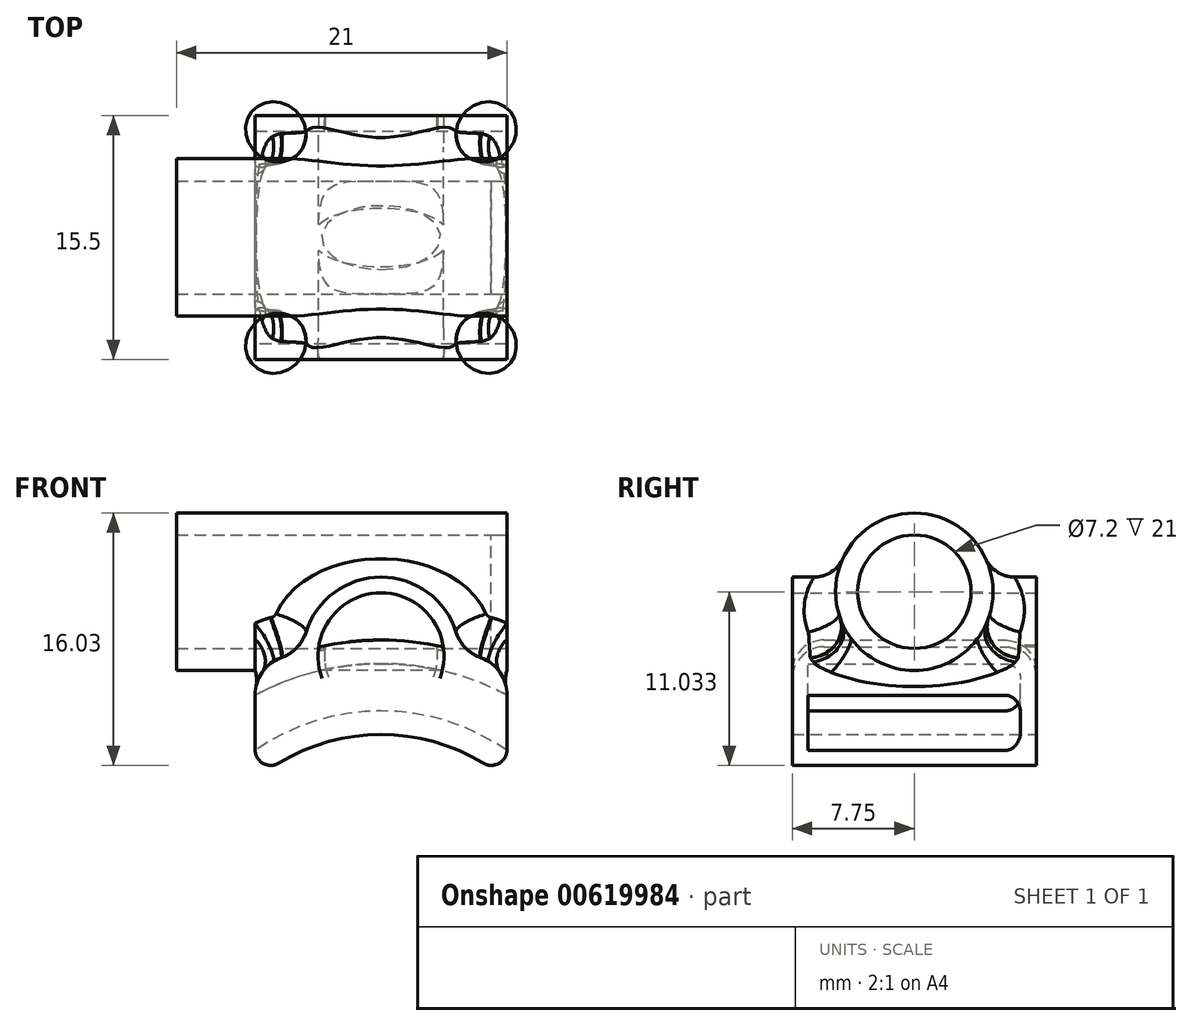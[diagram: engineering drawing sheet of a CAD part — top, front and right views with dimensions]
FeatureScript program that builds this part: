
annotation { "Feature Type Name" : "Feature", "Feature Type Description" : "" }
export const myFeature = defineFeature(function(context is Context, id is Id, definition is map)
    precondition{}
    {
        {
            var Q0;
            Q0=qCreatedBy(makeId("Front.planeOp"),FACE);
            var sketch = newSketch(context, id + "F0", { "sketchPlane" : qUnion([Q0])});
            skArc(sketch, "E0", {"start": v(8, 9.6) * mm, "mid": v(0, 12.5) * mm, "end": v(-8, 9.6) * mm});
            skArc(sketch, "E1.0", {"start": v(8, 11.49) * mm, "mid": v(0, 14) * mm, "end": v(-8, 11.49) * mm});
            skLineSegment(sketch, "E2", {"start": v(-8, 11.49) * mm, "end": v(-8, 9.6) * mm});
            skLineSegment(sketch, "E3", {"start": v(8, 11.49) * mm, "end": v(8, 9.6) * mm});
            skArc(sketch, "E4.0", {"start": v(8, 15) * mm, "mid": v(0, 17) * mm, "end": v(-8, 15) * mm});
            skLineSegment(sketch, "E5", {"start": v(-8, 15) * mm, "end": v(-8, 16.68) * mm});
            skLineSegment(sketch, "E6", {"start": v(8, 15) * mm, "end": v(8, 16.68) * mm});
            skArc(sketch, "E7.0", {"start": v(8, 16.68) * mm, "mid": v(0, 18.5) * mm, "end": v(-8, 16.68) * mm});
            skPoint(sketch, "E8.end.orphan", {"position": v(-8, 29.56) * mm});
            skPoint(sketch, "E8.start.orphan", {"position": v(8, 29.56) * mm});
            skArc(sketch, "E9", {"start": v(5, 17.81) * mm, "mid": v(0, 22.5) * mm, "end": v(-5, 17.81) * mm});
            skPoint(sketch, "E9.centerSnap0", {"position": v(0, 17) * mm});
            skArc(sketch, "E10.0", {"start": v(3.96, 18.07) * mm, "mid": v(0, 21.5) * mm, "end": v(-3.96, 18.07) * mm});
            skSolve(sketch);
        }
        {
            var Q0;
            Q0=qSketchRegion(id+"F0",true);
            extrude(context, id + "F1", {"entities" : qUnion([Q0]), "depth" : 13.5 * mm, "offsetDistance" : 25 * mm});
        }
        {
            var Q0;
            Q0=makeQuery(id+"F1.opExtrude","CAP_FACE",FACE,{"disambiguationData":[OSD([sQuery(id+"F0.wireOp",EDGE,"E0"),sQuery(id+"F0.wireOp",EDGE,"E1.0"),sQuery(id+"F0.wireOp",EDGE,"E2"),sQuery(id+"F0.wireOp",EDGE,"E3")])],"isStart":true});
            var sketch = newSketch(context, id + "F2", { "sketchPlane" : qUnion([Q0])});
            skCircle(sketch, "E11", {"center": v(0, 17.5) * mm, "radius": 3.6 * mm});
            skPoint(sketch, "E11.centerSnap0", {"position": v(0, 14) * mm});
            skCircle(sketch, "E12", {"center": v(0, 17.5) * mm, "radius": 5 * mm});
            skSolve(sketch);
        }
        {
            var Q0;
            Q0=qSketchRegion(id+"F2",true);
            extrude(context, id + "F3", {"entities" : qUnion([Q0]), "depth" : 1 * mm, "offsetDistance" : 25 * mm});
        }
        {
            var Q0;
            Q0=makeQuery(id+"F1.opExtrude","CAP_FACE",FACE,{"disambiguationData":[OSD([sQuery(id+"F0.wireOp",EDGE,"E4.0"),sQuery(id+"F0.wireOp",EDGE,"E5"),sQuery(id+"F0.wireOp",EDGE,"E6"),sQuery(id+"F0.wireOp",EDGE,"E7.0"),sQuery(id+"F0.wireOp",EDGE,"E9"),sQuery(id+"F0.wireOp",EDGE,"E10.0")])],"isStart":true});
            var sketch = newSketch(context, id + "F4", { "sketchPlane" : qUnion([Q0])});
            skArc(sketch, "E13.0", {"start": v(-3.54, 18.16) * mm, "mid": v(0, 13.9) * mm, "end": v(3.54, 18.16) * mm});
            skArc(sketch, "E14.0", {"start": v(-3.54, 18.16) * mm, "mid": v(0, 18.5) * mm, "end": v(3.54, 18.16) * mm});
            skSolve(sketch);
        }
        {
            var Q0;
            Q0=qSketchRegion(id+"F4",true);
            extrude(context, id + "F5", {"entities" : qUnion([Q0]), "depth" : 1 * mm, "offsetDistance" : 25 * mm});
        }
        {
            var Q0;
            Q0=makeQuery(id+"F1.opExtrude","CAP_FACE",FACE,{"disambiguationData":[OSD([sQuery(id+"F0.wireOp",EDGE,"E0"),sQuery(id+"F0.wireOp",EDGE,"E1.0"),sQuery(id+"F0.wireOp",EDGE,"E2"),sQuery(id+"F0.wireOp",EDGE,"E3")])],"isStart":true});
            var sketch = newSketch(context, id + "F6", { "sketchPlane" : qUnion([Q0])});
            skLineSegment(sketch, "E15.0", {"start": v(-8, 11.49) * mm, "end": v(-8, 9.6) * mm});
            skLineSegment(sketch, "E15.2", {"start": v(8, 9.6) * mm, "end": v(8, 11.49) * mm});
            skArc(sketch, "E15.3", {"start": v(-8, 9.6) * mm, "mid": v(0, 12.5) * mm, "end": v(8, 9.6) * mm});
            skArc(sketch, "E16.0", {"start": v(-8, 16.68) * mm, "mid": v(-6.52, 17.31) * mm, "end": v(-5, 17.81) * mm});
            skArc(sketch, "E17.0", {"start": v(5, 17.81) * mm, "mid": v(6.52, 17.31) * mm, "end": v(8, 16.68) * mm});
            skLineSegment(sketch, "E18.0", {"start": v(-8, 15) * mm, "end": v(-8, 16.68) * mm});
            skLineSegment(sketch, "E19.0", {"start": v(8, 15) * mm, "end": v(8, 16.68) * mm});
            skArc(sketch, "E20.0", {"start": v(-5, 17.81) * mm, "mid": v(0, 12.5) * mm, "end": v(5, 17.81) * mm});
            skLineSegment(sketch, "E21", {"start": v(-8, 15) * mm, "end": v(-8, 11.49) * mm});
            skLineSegment(sketch, "E22", {"start": v(8, 15) * mm, "end": v(8, 11.49) * mm});
            skSolve(sketch);
        }
        {
            var Q0;
            Q0=qSketchRegion(id+"F6",true);
            extrude(context, id + "F7", {"entities" : qUnion([Q0]), "depth" : 1 * mm, "offsetDistance" : 25 * mm});
        }
        {
            var Q0;
            Q0=makeQuery(id+"F1.opExtrude","CAP_FACE",FACE,{"disambiguationData":[OSD([sQuery(id+"F0.wireOp",EDGE,"E0"),sQuery(id+"F0.wireOp",EDGE,"E1.0"),sQuery(id+"F0.wireOp",EDGE,"E2"),sQuery(id+"F0.wireOp",EDGE,"E3")])],"isStart":false});
            var sketch = newSketch(context, id + "F8", { "sketchPlane" : qUnion([Q0])});
            skArc(sketch, "E23.0", {"start": v(8, 9.6) * mm, "mid": v(0, 12.5) * mm, "end": v(-8, 9.6) * mm});
            skArc(sketch, "E24.0", {"start": v(8, 16.68) * mm, "mid": v(0, 18.5) * mm, "end": v(-8, 16.68) * mm});
            skLineSegment(sketch, "E25", {"start": v(-8, 9.6) * mm, "end": v(-8, 16.68) * mm});
            skLineSegment(sketch, "E26", {"start": v(8, 9.6) * mm, "end": v(8, 16.68) * mm});
            skArc(sketch, "E27.0", {"start": v(5, 17.81) * mm, "mid": v(0, 22.5) * mm, "end": v(-5, 17.81) * mm});
            skArc(sketch, "E28.0", {"start": v(3.96, 18.07) * mm, "mid": v(0, 21.5) * mm, "end": v(-3.96, 18.07) * mm});
            skSolve(sketch);
        }
        {
            var Q0;
            Q0=qSketchRegion(id+"F8",true);
            extrude(context, id + "F9", {"entities" : qUnion([Q0]), "depth" : 1 * mm, "offsetDistance" : 25 * mm});
        }
        {
            var Q0;
            Q0=makeQuery(id+"F1.opExtrude","SWEPT_BODY",BODY,{"disambiguationData":[OSD([sQuery(id+"F0.wireOp",EDGE,"E4.0"),sQuery(id+"F0.wireOp",EDGE,"E5"),sQuery(id+"F0.wireOp",EDGE,"E6"),sQuery(id+"F0.wireOp",EDGE,"E7.0"),sQuery(id+"F0.wireOp",EDGE,"E9"),sQuery(id+"F0.wireOp",EDGE,"E10.0")])]});
            var Q1;
            Q1=makeQuery(id+"F3.opExtrude","SWEPT_BODY",BODY,{"disambiguationData":[OSD([sQuery(id+"F2.wireOp",EDGE,"E11"),sQuery(id+"F2.wireOp",EDGE,"E12")])]});
            var Q2;
            Q2=makeQuery(id+"F1.opExtrude","SWEPT_BODY",BODY,{"disambiguationData":[OSD([sQuery(id+"F0.wireOp",EDGE,"E0"),sQuery(id+"F0.wireOp",EDGE,"E1.0"),sQuery(id+"F0.wireOp",EDGE,"E2"),sQuery(id+"F0.wireOp",EDGE,"E3")])]});
            var Q3;
            Q3=makeQuery(id+"F7.opExtrude","SWEPT_BODY",BODY,{"disambiguationData":[OSD([sQuery(id+"F6.wireOp",EDGE,"E15.2"),sQuery(id+"F6.wireOp",EDGE,"E15.3"),sQuery(id+"F6.wireOp",EDGE,"E17.0"),sQuery(id+"F6.wireOp",EDGE,"E19.0"),sQuery(id+"F6.wireOp",EDGE,"E20.0"),sQuery(id+"F6.wireOp",EDGE,"E22")])]});
            var Q4;
            Q4=makeQuery(id+"F7.opExtrude","SWEPT_BODY",BODY,{"disambiguationData":[OSD([sQuery(id+"F6.wireOp",EDGE,"E15.0"),sQuery(id+"F6.wireOp",EDGE,"E15.3"),sQuery(id+"F6.wireOp",EDGE,"E16.0"),sQuery(id+"F6.wireOp",EDGE,"E18.0"),sQuery(id+"F6.wireOp",EDGE,"E20.0"),sQuery(id+"F6.wireOp",EDGE,"E21")])]});
            var Q5;
            Q5=makeQuery(id+"F5.opExtrude","SWEPT_BODY",BODY,{"disambiguationData":[OSD([sQuery(id+"F4.wireOp",EDGE,"E13.0"),sQuery(id+"F4.wireOp",EDGE,"E14.0")])]});
            var Q6;
            Q6=makeQuery(id+"F9.opExtrude","SWEPT_BODY",BODY,{"disambiguationData":[OSD([sQuery(id+"F8.wireOp",EDGE,"E23.0"),sQuery(id+"F8.wireOp",EDGE,"E24.0"),sQuery(id+"F8.wireOp",EDGE,"E25"),sQuery(id+"F8.wireOp",EDGE,"E26")])]});
            booleanBodies(context, id + "F10", {"operationType" : BooleanOperationType.UNION, "tools" : qUnion([Q0, Q1, Q2, Q3, Q4, Q5, Q6])});
        }
        {
            var Q0;
            Q0=makeQuery(id+"F5.opExtrude","CAP_EDGE",EDGE,{"disambiguationData":[OSD([sQuery(id+"F4.wireOp",EDGE,"E14.0")])],"isStart":false});
            var Q1;
            {var subQ0=sQuery(id+"F8.wireOp",EDGE,"E28.0");var subQ1=sQuery(id+"F8.wireOp",EDGE,"E24.0");Q1=makeQuery(id+"F9.opExtrude","CAP_EDGE",EDGE,{"disambiguationData":[OSD([subQ1]),TDD([makeQuery(id+"F8.imprint","IMPRINT",EDGE,{"disambiguationData":[TD([[makeQuery(id+"F8.imprint","INTERSECT",VERTEX,{"disambiguationData":[OD(0.0)],"derivedFrom":[subQ1,subQ0]}),-1.0]])],"derivedFrom":subQ1})])],"isStart":false});}
            fillet(context, id + "F11", {"entities" : qUnion([Q0, Q1]), "radius" : 2 * mm, "tangentPropagation" : true, "allowEdgeOverflow" : false});
        }
        {
            var Q0;
            {var subQ0=sQuery(id+"F0.wireOp",EDGE,"E9");var subQ1=sQuery(id+"F0.wireOp",EDGE,"E7.0");Q0=makeQuery(id+"F10.opBoolean","MERGE",EDGE,{"derivedFrom":[makeQuery(id+"F1.opExtrude","SWEPT_EDGE",EDGE,{"disambiguationData":[OSD([subQ1,subQ0]),TDD([makeQuery(id+"F0.imprint","INTERSECT",VERTEX,{"disambiguationData":[OD(1.0)],"derivedFrom":[subQ1,subQ0]})])]}),makeQuery(id+"F7.opExtrude","SWEPT_EDGE",EDGE,{"disambiguationData":[OSD([sQuery(id+"F6.wireOp",EDGE,"E17.0"),sQuery(id+"F6.wireOp",EDGE,"E20.0")])]})]});}
            var Q1;
            Q1=makeQuery(id+"F10.opBoolean","MERGE",EDGE,{"derivedFrom":[makeQuery(id+"F1.opExtrude","SWEPT_EDGE",EDGE,{"disambiguationData":[OSD([sQuery(id+"F0.wireOp",EDGE,"E5"),sQuery(id+"F0.wireOp",EDGE,"E7.0")])]}),makeQuery(id+"F7.opExtrude","SWEPT_EDGE",EDGE,{"disambiguationData":[OSD([sQuery(id+"F6.wireOp",EDGE,"E17.0"),sQuery(id+"F6.wireOp",EDGE,"E19.0")])]}),makeQuery(id+"F9.opExtrude","SWEPT_EDGE",EDGE,{"disambiguationData":[OSD([sQuery(id+"F8.wireOp",EDGE,"E24.0"),sQuery(id+"F8.wireOp",EDGE,"E25")])]})]});
            var Q2;
            {var subQ0=sQuery(id+"F0.wireOp",EDGE,"E9");var subQ1=sQuery(id+"F0.wireOp",EDGE,"E7.0");Q2=makeQuery(id+"F10.opBoolean","MERGE",EDGE,{"derivedFrom":[makeQuery(id+"F1.opExtrude","SWEPT_EDGE",EDGE,{"disambiguationData":[OSD([subQ1,subQ0]),TDD([makeQuery(id+"F0.imprint","INTERSECT",VERTEX,{"disambiguationData":[OD(0.0)],"derivedFrom":[subQ1,subQ0]})])]}),makeQuery(id+"F7.opExtrude","SWEPT_EDGE",EDGE,{"disambiguationData":[OSD([sQuery(id+"F6.wireOp",EDGE,"E16.0"),sQuery(id+"F6.wireOp",EDGE,"E20.0")])]})]});}
            var Q3;
            Q3=makeQuery(id+"F10.opBoolean","MERGE",EDGE,{"derivedFrom":[makeQuery(id+"F1.opExtrude","SWEPT_EDGE",EDGE,{"disambiguationData":[OSD([sQuery(id+"F0.wireOp",EDGE,"E6"),sQuery(id+"F0.wireOp",EDGE,"E7.0")])]}),makeQuery(id+"F7.opExtrude","SWEPT_EDGE",EDGE,{"disambiguationData":[OSD([sQuery(id+"F6.wireOp",EDGE,"E16.0"),sQuery(id+"F6.wireOp",EDGE,"E18.0")])]}),makeQuery(id+"F9.opExtrude","SWEPT_EDGE",EDGE,{"disambiguationData":[OSD([sQuery(id+"F8.wireOp",EDGE,"E24.0"),sQuery(id+"F8.wireOp",EDGE,"E26")])]})]});
            fillet(context, id + "F12", {"entities" : qUnion([Q0, Q1, Q2, Q3]), "radius" : 2.5 * mm, "tangentPropagation" : true, "allowEdgeOverflow" : false});
        }
        {
            var Q0;
            Q0=makeQuery(id+"F10.opBoolean","MERGE",EDGE,{"derivedFrom":[makeQuery(id+"F1.opExtrude","SWEPT_EDGE",EDGE,{"disambiguationData":[OSD([sQuery(id+"F0.wireOp",EDGE,"E0"),sQuery(id+"F0.wireOp",EDGE,"E2")])]}),makeQuery(id+"F7.opExtrude","SWEPT_EDGE",EDGE,{"disambiguationData":[OSD([sQuery(id+"F6.wireOp",EDGE,"E15.2"),sQuery(id+"F6.wireOp",EDGE,"E15.3")])]}),makeQuery(id+"F9.opExtrude","SWEPT_EDGE",EDGE,{"disambiguationData":[OSD([sQuery(id+"F8.wireOp",EDGE,"E23.0"),sQuery(id+"F8.wireOp",EDGE,"E25")])]})]});
            var Q1;
            Q1=makeQuery(id+"F10.opBoolean","MERGE",EDGE,{"derivedFrom":[makeQuery(id+"F1.opExtrude","SWEPT_EDGE",EDGE,{"disambiguationData":[OSD([sQuery(id+"F0.wireOp",EDGE,"E0"),sQuery(id+"F0.wireOp",EDGE,"E3")])]}),makeQuery(id+"F7.opExtrude","SWEPT_EDGE",EDGE,{"disambiguationData":[OSD([sQuery(id+"F6.wireOp",EDGE,"E15.0"),sQuery(id+"F6.wireOp",EDGE,"E15.3")])]}),makeQuery(id+"F9.opExtrude","SWEPT_EDGE",EDGE,{"disambiguationData":[OSD([sQuery(id+"F8.wireOp",EDGE,"E23.0"),sQuery(id+"F8.wireOp",EDGE,"E26")])]})]});
            fillet(context, id + "F13", {"entities" : qUnion([Q0, Q1]), "radius" : 1 * mm, "tangentPropagation" : true, "allowEdgeOverflow" : false});
        }
        {
            var Q0;
            {var subQ0=sQuery(id+"F6.wireOp",EDGE,"E20.0");var subQ1=sQuery(id+"F6.wireOp",EDGE,"E15.3");Q0=makeQuery(id+"F10.opBoolean","INTERSECT",EDGE,{"derivedFrom":[makeQuery(id+"F3.opExtrude","CAP_FACE",FACE,{"disambiguationData":[OSD([sQuery(id+"F2.wireOp",EDGE,"E11"),sQuery(id+"F2.wireOp",EDGE,"E12")])],"isStart":true}),makeQuery(id+"F5.opExtrude","CAP_FACE",FACE,{"disambiguationData":[OSD([sQuery(id+"F4.wireOp",EDGE,"E13.0"),sQuery(id+"F4.wireOp",EDGE,"E14.0")])],"isStart":true}),makeQuery(id+"F7.opExtrude","CAP_FACE",FACE,{"disambiguationData":[OSD([sQuery(id+"F6.wireOp",EDGE,"E15.0"),subQ1,sQuery(id+"F6.wireOp",EDGE,"E16.0"),sQuery(id+"F6.wireOp",EDGE,"E18.0"),subQ0,sQuery(id+"F6.wireOp",EDGE,"E21")])],"isStart":true}),makeQuery(id+"F7.opExtrude","CAP_FACE",FACE,{"disambiguationData":[OSD([sQuery(id+"F6.wireOp",EDGE,"E15.2"),subQ1,sQuery(id+"F6.wireOp",EDGE,"E17.0"),sQuery(id+"F6.wireOp",EDGE,"E19.0"),subQ0,sQuery(id+"F6.wireOp",EDGE,"E22")])],"isStart":true})]});}
            var Q1;
            Q1=makeQuery(id+"F1.opExtrude","CAP_EDGE",EDGE,{"disambiguationData":[OSD([sQuery(id+"F0.wireOp",EDGE,"E4.0")])],"isStart":true});
            var Q2;
            Q2=makeQuery(id+"F1.opExtrude","CAP_EDGE",EDGE,{"disambiguationData":[OSD([sQuery(id+"F0.wireOp",EDGE,"E1.0")])],"isStart":false});
            var Q3;
            Q3=makeQuery(id+"F1.opExtrude","CAP_EDGE",EDGE,{"disambiguationData":[OSD([sQuery(id+"F0.wireOp",EDGE,"E4.0")])],"isStart":false});
            fillet(context, id + "F14", {"entities" : qUnion([Q0, Q1, Q2, Q3]), "radius" : 1 * mm, "tangentPropagation" : true, "allowEdgeOverflow" : false});
        }
        {
            var Q0;
            Q0=qCreatedBy(makeId("Right.planeOp"),FACE);
            var sketch = newSketch(context, id + "F15", { "sketchPlane" : qUnion([Q0])});
            skCircle(sketch, "E29", {"center": v(-6.75, 21.57) * mm, "radius": 5 * mm});
            skSolve(sketch);
        }
        {
            var Q0;
            Q0=qSketchRegion(id+"F15",true);
            extrude(context, id + "F16", {"entities" : qUnion([Q0]), "operationType" : NewBodyOperationType.ADD, "endBound" : BoundingType.SYMMETRIC, "depth" : 16 * mm, "offsetDistance" : 25 * mm});
        }
        {
            var Q0;
            Q0=makeQuery(id+"F16.opExtrude","CAP_FACE",FACE,{"disambiguationData":[OSD([sQuery(id+"F15.wireOp",EDGE,"E29")])],"isStart":false});
            var sketch = newSketch(context, id + "F17", { "sketchPlane" : qUnion([Q0])});
            skCircle(sketch, "E30", {"center": v(-6.75, 21.57) * mm, "radius": 3.6 * mm});
            skSolve(sketch);
        }
        {
            var Q0;
            Q0=qSketchRegion(id+"F17",true);
            extrude(context, id + "F18", {"entities" : qUnion([Q0]), "operationType" : NewBodyOperationType.REMOVE, "endBound" : BoundingType.THROUGH_ALL, "oppositeDirection" : true, "depth" : 25 * mm, "offsetDistance" : 25 * mm});
        }
        {
            var Q0;
            Q0=makeQuery(id+"F9.opExtrude","CAP_FACE",FACE,{"disambiguationData":[OSD([sQuery(id+"F8.wireOp",EDGE,"E23.0"),sQuery(id+"F8.wireOp",EDGE,"E24.0"),sQuery(id+"F8.wireOp",EDGE,"E25"),sQuery(id+"F8.wireOp",EDGE,"E26"),sQuery(id+"F8.wireOp",EDGE,"E27.0"),sQuery(id+"F8.wireOp",EDGE,"E28.0")])],"isStart":false});
            var sketch = newSketch(context, id + "F19", { "sketchPlane" : qUnion([Q0])});
            skLineSegment(sketch, "E31", {"start": v(0, 27.62) * mm, "end": v(0, 5.28) * mm});
            skArc(sketch, "E32.0", {"start": v(-3.96, 18.07) * mm, "mid": v(0, 18.5) * mm, "end": v(3.96, 18.07) * mm});
            skArc(sketch, "E33.0", {"start": v(3.96, 18.07) * mm, "mid": v(0, 21.5) * mm, "end": v(-3.96, 18.07) * mm});
            skSolve(sketch);
        }
        {
            var Q0;
            Q0=qSketchRegion(id+"F19",true);
            extrude(context, id + "F20", {"entities" : qUnion([Q0]), "operationType" : NewBodyOperationType.REMOVE, "endBound" : BoundingType.THROUGH_ALL, "oppositeDirection" : true, "depth" : 25 * mm, "offsetDistance" : 25 * mm});
        }
        {
            var Q0;
            Q0=makeQuery(id+"F16.boolean.opBoolean","INTERSECT",EDGE,{"disambiguationData":[OD(1.0)],"derivedFrom":[makeQuery(id+"F10.opBoolean","MERGE",FACE,{"derivedFrom":[makeQuery(id+"F1.opExtrude","SWEPT_FACE",FACE,{"disambiguationData":[OSD([sQuery(id+"F0.wireOp",EDGE,"E9")])]}),makeQuery(id+"F3.opExtrude","SWEPT_FACE",FACE,{"disambiguationData":[OSD([sQuery(id+"F2.wireOp",EDGE,"E12")])]}),makeQuery(id+"F9.opExtrude","SWEPT_FACE",FACE,{"disambiguationData":[OSD([sQuery(id+"F8.wireOp",EDGE,"E27.0")])]})]}),makeQuery(id+"F16.opExtrude","SWEPT_FACE",FACE,{"disambiguationData":[OSD([sQuery(id+"F15.wireOp",EDGE,"E29")])]})]});
            fillet(context, id + "F21", {"entities" : qUnion([Q0]), "radius" : 2 * mm, "tangentPropagation" : true, "allowEdgeOverflow" : false});
        }
        {
            var Q0;
            Q0=makeQuery(id+"F16.opExtrude","CAP_FACE",FACE,{"disambiguationData":[OSD([sQuery(id+"F15.wireOp",EDGE,"E29")])],"isStart":false});
            var sketch = newSketch(context, id + "F22", { "sketchPlane" : qUnion([Q0])});
            skCircle(sketch, "E34.0", {"center": v(-6.75, 21.57) * mm, "radius": 3.6 * mm});
            skSolve(sketch);
        }
        {
            var Q0;
            Q0 = qSketchRegion(id + "F22", true);
            extrude(context, id + "F23", {"entities" : qUnion([Q0]), "oppositeDirection" : true, "depth" : 1 * mm, "offsetDistance" : 25 * mm});
        }
        {
            var Q0;
            Q0=makeQuery(id+"F16.opExtrude","CAP_FACE",FACE,{"disambiguationData":[OSD([sQuery(id+"F15.wireOp",EDGE,"E29")])],"isStart":true});
            var sketch = newSketch(context, id + "F24", { "sketchPlane" : qUnion([Q0])});
            skCircle(sketch, "E35.0", {"center": v(6.75, 21.57) * mm, "radius": 3.6 * mm});
            skCircle(sketch, "E36", {"center": v(6.75, 21.57) * mm, "radius": 5 * mm});
            skSolve(sketch);
        }
        {
            var Q0;
            Q0 = qSketchRegion(id + "F24", true);
            extrude(context, id + "F25", {"entities" : qUnion([Q0]), "operationType" : NewBodyOperationType.ADD, "depth" : 5 * mm, "offsetDistance" : 25 * mm});
        }
    });
